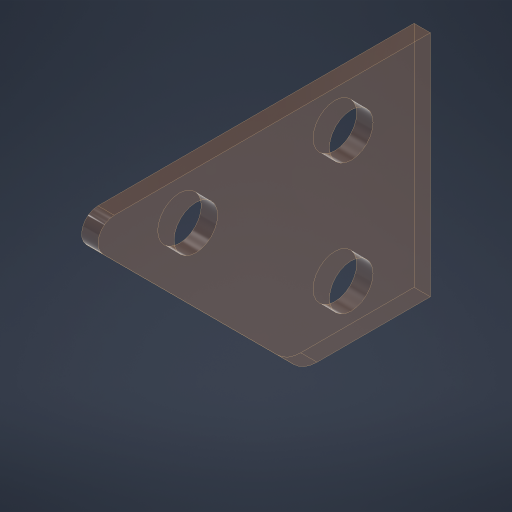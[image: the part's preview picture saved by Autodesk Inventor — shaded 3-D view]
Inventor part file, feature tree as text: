
AUTODESK INVENTOR PART (.ipt)
format: ipt  version: 2024 (Build 280153000, 153)  size: 249,856 bytes
history: native  units: in
note: dims shown in document units (in); Inventor stores cm internally (conversion verified against a paired STEP export)
features: sketch x3, extrude x1, hole x1, split x1
ambient origin geometry x8: Origin, YZ Plane, XZ Plane, XY Plane, X Axis, Y Axis, Z Axis, Center Point
bodies: Solid1 (feature_tree)
feature tree (6):
  extrude  "Extrusion1"  Depth=0.125in
  hole  "Hole1"  [1 undecoded]
  split  "Split1"
  sketch  "Sketch1"  dims[d1=0.875in d6=0.125in]
  sketch  "Sketch2"  dims[d7=0.0625in d8=0.0in d13=0.1875in]
  sketch  "Sketch3"  dims[d14=0.5in d15=0.25in d16=0.5in d17=0.167in d18=0.75in d19=0.375in d20=0.25in d21=0.5635in d22=1.0in d23=0.8108in d46=0.0625in d47=0.125in d49=0.188in d50=45.0deg d51=0.403in d52=45.0deg]
note: 1 required parameter value undecoded (feature->parameter linkage not recoverable at this tier; creation-order binding heuristic only, values carry confidence <= 0.55)
